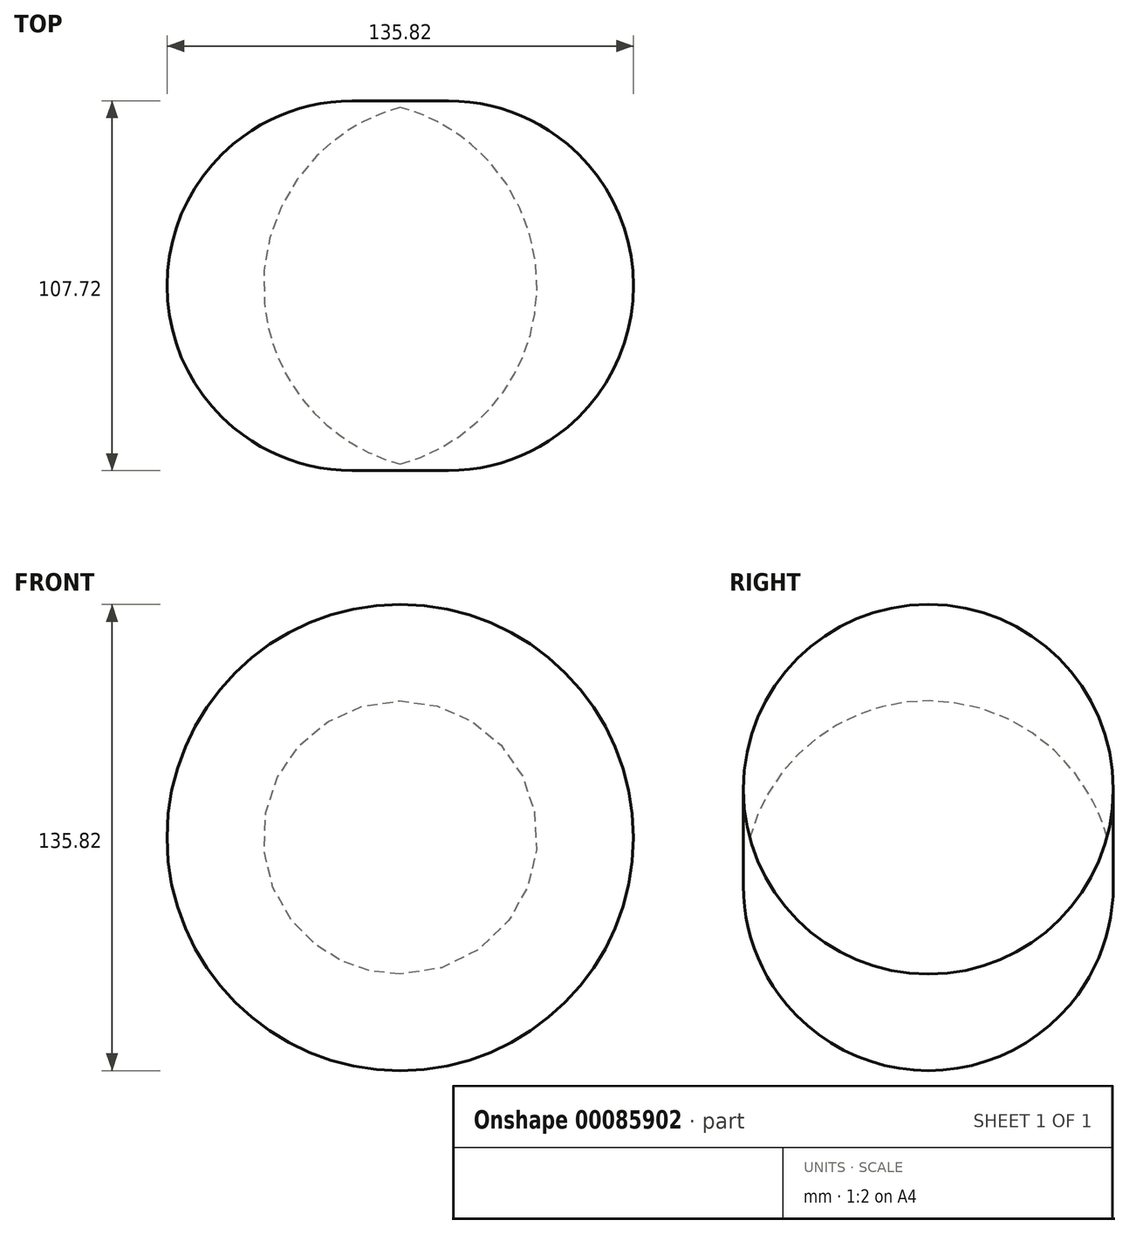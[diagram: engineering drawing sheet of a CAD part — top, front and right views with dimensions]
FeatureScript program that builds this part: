
annotation { "Feature Type Name" : "Feature", "Feature Type Description" : "" }
export const myFeature = defineFeature(function(context is Context, id is Id, definition is map)
    precondition{}
    {
        {
            var Q0;
            Q0=qCreatedBy(makeId("Top.planeOp"),FACE);
            var sketch = newSketch(context, id + "F0", { "sketchPlane" : qUnion([Q0])});
            skLineSegment(sketch, "E0", {"start": v(-32.18, 56.47) * mm, "end": v(-32.18, -47.53) * mm});
            skArc(sketch, "E1", {"start": v(-32.18, -47.53) * mm, "mid": v(7.63, 4.47) * mm, "end": v(-32.18, 56.47) * mm});
            skSolve(sketch);
        }
        {
            var Q0;
            Q0=makeQuery(id+"F0.imprint","IMPRINT",FACE,{"disambiguationData":[TD([[makeQuery(id+"F0.imprint","IMPRINT",EDGE,{"derivedFrom":sQuery(id+"F0.wireOp",EDGE,"E0")}),1.0]])]});
            var Q1;
            Q1=sQuery(id+"F0.wireOp",EDGE,"E0");
            revolve(context, id + "F1", {"entities" : qUnion([Q0]), "axis" : qUnion([Q1]), "revolveType" : RevolveType.FULL});
        }
    });
